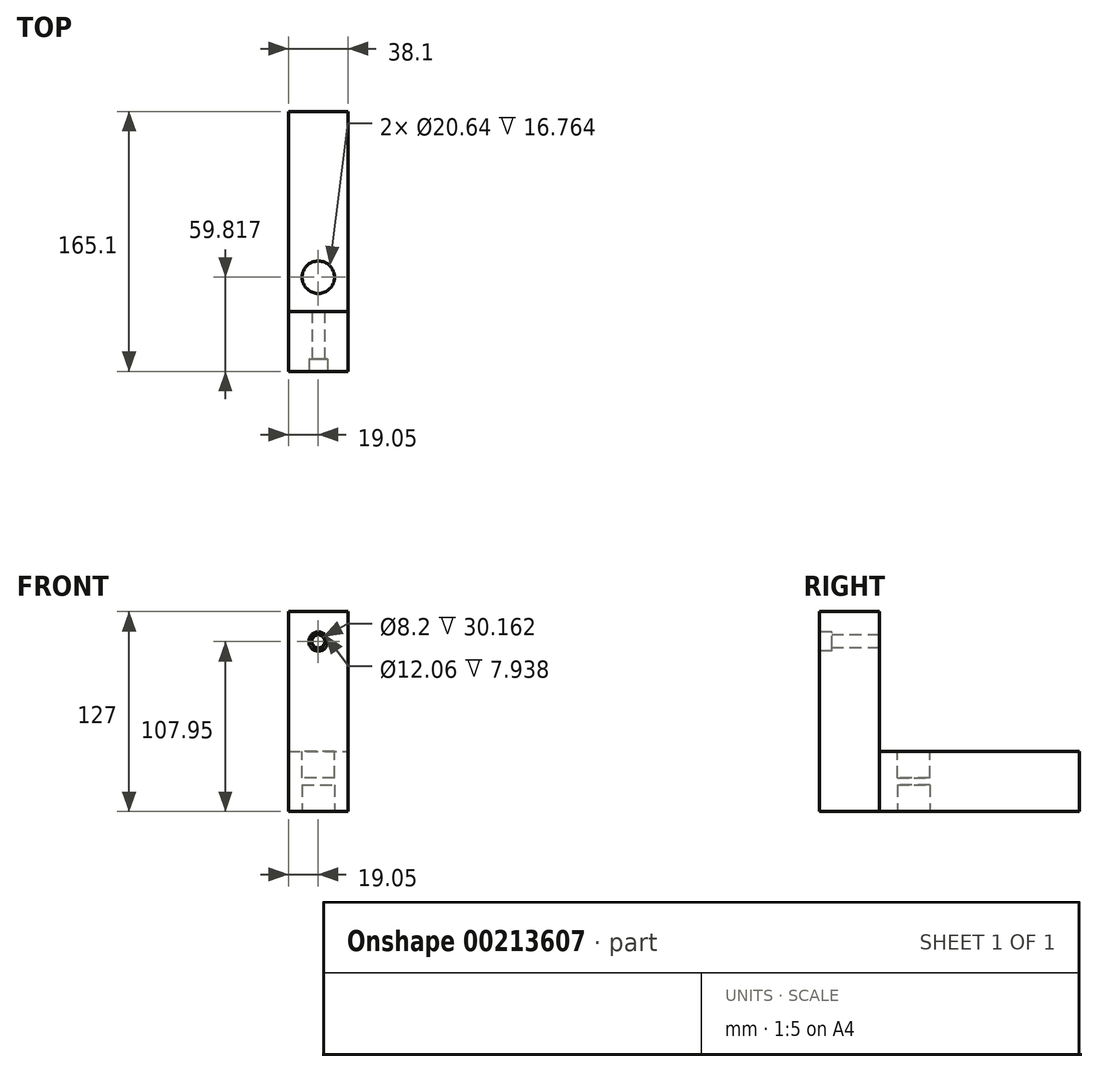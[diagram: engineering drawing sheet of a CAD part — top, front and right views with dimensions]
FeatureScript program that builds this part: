
annotation { "Feature Type Name" : "Feature", "Feature Type Description" : "" }
export const myFeature = defineFeature(function(context is Context, id is Id, definition is map)
    precondition{}
    {
        {
            var Q0;
            Q0=qCreatedBy(makeId("Front.planeOp"),FACE);
            var sketch = newSketch(context, id + "F0", { "sketchPlane" : qUnion([Q0])});
            skLineSegment(sketch, "E0.bottom", {"start": v(0, 0) * mm, "end": v(38.1, 0) * mm});
            skLineSegment(sketch, "E0.top", {"start": v(0, 127) * mm, "end": v(38.1, 127) * mm});
            skLineSegment(sketch, "E0.left", {"start": v(0, 0) * mm, "end": v(0, 127) * mm});
            skLineSegment(sketch, "E0.right", {"start": v(38.1, 0) * mm, "end": v(38.1, 127) * mm});
            skSolve(sketch);
        }
        {
            var Q0;
            Q0 = qSketchRegion(id + "F0", true);
            extrude(context, id + "F1", {"entities" : qUnion([Q0]), "depth" : 38.1 * mm});
        }
        {
            var Q0;
            Q0=makeQuery(id+"F1.opExtrude","SWEPT_FACE",FACE,{"disambiguationData":[OSD([sQuery(id+"F0.wireOp",EDGE,"E0.right")])]});
            var sketch = newSketch(context, id + "F2", { "sketchPlane" : qUnion([Q0])});
            skLineSegment(sketch, "E1.bottom", {"start": v(127, 0) * mm, "end": v(0, 0) * mm});
            skLineSegment(sketch, "E1.top", {"start": v(127, 38.1) * mm, "end": v(0, 38.1) * mm});
            skLineSegment(sketch, "E1.left", {"start": v(0, 0) * mm, "end": v(0, 38.1) * mm});
            skLineSegment(sketch, "E1.right", {"start": v(127, 0) * mm, "end": v(127, 38.1) * mm});
            skSolve(sketch);
        }
        {
            var Q0;
            Q0 = qSketchRegion(id + "F2", true);
            extrude(context, id + "F3", {"entities" : qUnion([Q0]), "oppositeDirection" : true, "depth" : 38.1 * mm});
        }
        {
            var Q0;
            Q0=makeQuery(id+"F1.opExtrude","CAP_FACE",FACE,{"disambiguationData":[OSD([sQuery(id+"F0.wireOp",EDGE,"E0.bottom"),sQuery(id+"F0.wireOp",EDGE,"E0.top"),sQuery(id+"F0.wireOp",EDGE,"E0.left"),sQuery(id+"F0.wireOp",EDGE,"E0.right")])],"isStart":false});
            var sketch = newSketch(context, id + "F4", { "sketchPlane" : qUnion([Q0])});
            skCircle(sketch, "E2", {"center": v(19.05, 107.95) * mm, "radius": 4.1 * mm});
            skSolve(sketch);
        }
        {
            var Q0;
            Q0=sQuery(id+"F4.wireOp",VERTEX,"E2.center");
            var Q1;
            Q1=makeQuery(id+"F1.opExtrude","SWEPT_BODY",BODY,{"disambiguationData":[OSD([sQuery(id+"F0.wireOp",EDGE,"E0.bottom"),sQuery(id+"F0.wireOp",EDGE,"E0.top"),sQuery(id+"F0.wireOp",EDGE,"E0.left"),sQuery(id+"F0.wireOp",EDGE,"E0.right")])]});
            hole(context, id + "F5", {"style" : HoleStyle.C_BORE, "endStyle" : HoleEndStyle.THROUGH, "holeDiameter" : 8.2 * mm, "cBoreDiameter" : 12.06 * mm, "cBoreDepth" : 7.94 * mm, "locations" : qUnion([Q0]), "scope" : qUnion([Q1]), "isTappedThrough" : true});
        }
        {
            var Q0;
            Q0=makeQuery(id+"F3.opExtrude","SWEPT_FACE",FACE,{"disambiguationData":[OSD([sQuery(id+"F2.wireOp",EDGE,"E1.top")])]});
            var sketch = newSketch(context, id + "F6", { "sketchPlane" : qUnion([Q0])});
            skCircle(sketch, "E3", {"center": v(19.05, 21.72) * mm, "radius": 10.32 * mm});
            skSolve(sketch);
        }
        {
            var Q0;
            Q0 = qSketchRegion(id + "F6", true);
            extrude(context, id + "F7", {"entities" : qUnion([Q0]), "operationType" : NewBodyOperationType.REMOVE, "oppositeDirection" : true, "depth" : 16.76 * mm});
        }
        {
            var Q0;
            Q0=makeQuery(id+"F3.opExtrude","SWEPT_FACE",FACE,{"disambiguationData":[OSD([sQuery(id+"F2.wireOp",EDGE,"E1.bottom")])]});
            var sketch = newSketch(context, id + "F8", { "sketchPlane" : qUnion([Q0])});
            skCircle(sketch, "E4.0", {"center": v(19.05, -21.72) * mm, "radius": 10.32 * mm});
            skSolve(sketch);
        }
        {
            var Q0;
            Q0 = qSketchRegion(id + "F8", true);
            extrude(context, id + "F9", {"entities" : qUnion([Q0]), "operationType" : NewBodyOperationType.REMOVE, "oppositeDirection" : true, "depth" : 16.76 * mm});
        }
    });
